# Revit family: 111213017025804
name_source: partatom
category: Modelos genéricos
revit_build: Autodesk Revit 2018 (Build: 20190510_1515(x64)
units: mm (PartAtom-declared; Revit-internal decimal feet)

## family parameters
Compartido = No
Corte con vacíos al cargar = No
Cota de conector redondo = Diámetro de uso
Puede alojar armadura = No
Punto de cálculo de habitación = No
Se basa en plano de trabajo = No
Siempre vertical = No
Tipo de pieza = Normal

## types (1)
- GRADA ESTRIADA GOMA 320X4MM NEGRO TIRA 1.5MT
    Alto = 45 mm  [stored 0.147638 ft]
    Aplicacion = Escaleras
    Color = Negro
    Descripción = Grada Estriada 320x45 MM.
    Dimension = 320 mm  [stored 1.04987 ft]
    Dureza = 80 shore A
    Empresa = CNP SPA.
    Espesor = 4 mm  [stored 0.0131234 ft]
    Largo = 1500 mm  [stored 4.92126 ft]
    Material = PVC flexible negro
    Modelo = GRADA ESTRIADA GOMA 320X4MM
    Nombre SKU = GRADA ESTRIADA GOMA 320X4MM NEGRO TIRA 1.5MT
    Num SKUs = 111213017025804
    URL = https://www.empresascnp.cl
    Unidad = Tiras de 1.20 Mts y 1.50 Mts.
    Url Ficha tecnica = https://empresascnp.cl
    Uso = Gradas de goma son fabricadas en caucho SBR/Natural, ideal para zonas de alto
tráfico con diseño . El diseño Bi-Color permite divisar a distancia los escalones para
prevenir accidentes.
    Ventajas = Autoextinguible

note: [stored X ft] marks values corroborated as IEEE doubles in the binary element streams (Revit-internal decimal feet)

## geometry (parser evidence)
native form markers: Sweep x2
no freeform markers — native parametric forms only
